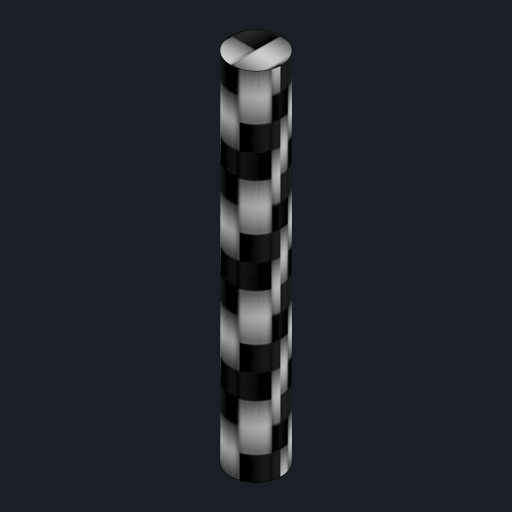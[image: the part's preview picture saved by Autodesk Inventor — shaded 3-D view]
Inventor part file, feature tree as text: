
AUTODESK INVENTOR PART (.ipt)
format: ipt  version: 2023 (Build 270158000, 158)  size: 122,880 bytes
history: native  units: mm
features: other x1, extrude x1, sketch x1
ambient origin geometry x8: Origin, YZ Plane, XZ Plane, XY Plane, X Axis, Y Axis, Z Axis, Center Point
bodies: Body1 (feature_tree)
feature tree (3):
  other  "ソリッド1"
  extrude  "押し出し1"  Depth=2.0mm
  sketch  "スケッチ1"
